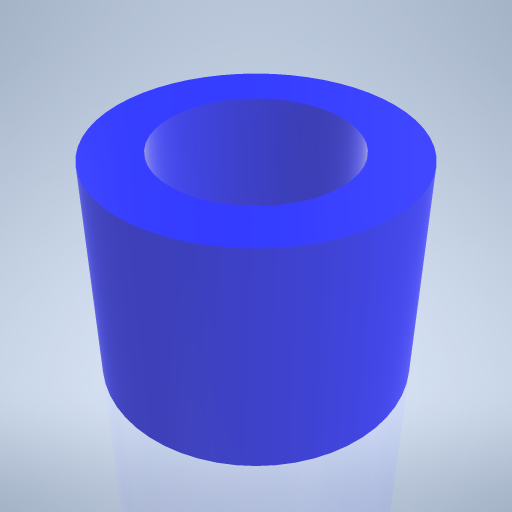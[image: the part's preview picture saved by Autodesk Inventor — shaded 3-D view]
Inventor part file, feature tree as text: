
AUTODESK INVENTOR PART (.ipt)
format: ipt  version: 2024.2 (Build 282272000, 272)  size: 213,504 bytes
history: native  units: mm
features: extrude x1, sketch x1
ambient origin geometry x8: Origin, YZ Plane, XZ Plane, XY Plane, X Axis, Y Axis, Z Axis, Center Point
bodies: Volumenkörper1 (feature_tree)
feature tree (2):
  extrude  "Extrusion1"  Depth=6.0mm
  sketch  "Skizze1"  dims[d0=8.0mm d1=5.0mm d2=6.0mm d3=0.0mm]
